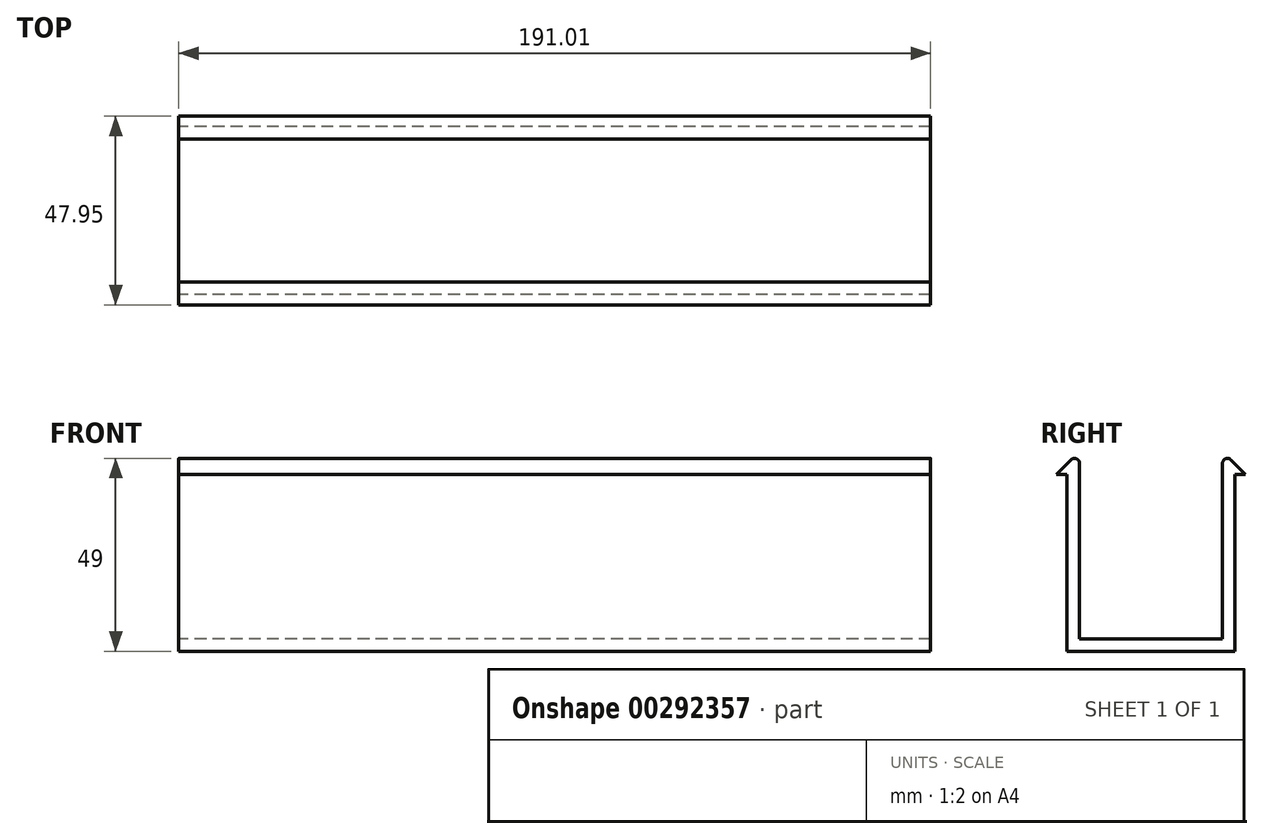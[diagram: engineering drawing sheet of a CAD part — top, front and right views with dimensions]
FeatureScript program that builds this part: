
annotation { "Feature Type Name" : "Feature", "Feature Type Description" : "" }
export const myFeature = defineFeature(function(context is Context, id is Id, definition is map)
    precondition{}
    {
        {
            var Q0;
            Q0=qCreatedBy(makeId("Right.planeOp"),FACE);
            var sketch = newSketch(context, id + "F0", { "sketchPlane" : qUnion([Q0])});
            skLineSegment(sketch, "E0", {"start": v(0, 0) * mm, "end": v(42.67, 0) * mm});
            skLineSegment(sketch, "E1", {"start": v(42.67, 0) * mm, "end": v(42.67, 44.98) * mm});
            skLineSegment(sketch, "E2", {"start": v(42.67, 44.98) * mm, "end": v(45.31, 44.98) * mm});
            skLineSegment(sketch, "E3", {"start": v(45.31, 44.98) * mm, "end": v(39.5, 50.8) * mm});
            skLineSegment(sketch, "E4", {"start": v(39.5, 50.8) * mm, "end": v(39.5, 3.18) * mm});
            skLineSegment(sketch, "E5", {"start": v(39.5, 3.18) * mm, "end": v(3.17, 3.17) * mm});
            skLineSegment(sketch, "E6", {"start": v(3.17, 3.17) * mm, "end": v(3.17, 50.8) * mm});
            skLineSegment(sketch, "E7", {"start": v(3.17, 50.8) * mm, "end": v(-2.64, 44.98) * mm});
            skLineSegment(sketch, "E8", {"start": v(-2.64, 44.98) * mm, "end": v(0, 44.98) * mm});
            skLineSegment(sketch, "E9", {"start": v(0, 44.98) * mm, "end": v(0, 0) * mm});
            skSolve(sketch);
        }
        {
            var Q0;
            Q0 = qSketchRegion(id + "F0", true);
            extrude(context, id + "F1", {"entities" : qUnion([Q0]), "depth" : 191 * mm});
        }
        {
            var Q0;
            Q0=makeQuery(id+"F1.opExtrude","SWEPT_EDGE",EDGE,{"disambiguationData":[OSD([sQuery(id+"F0.wireOp",EDGE,"E6"),sQuery(id+"F0.wireOp",EDGE,"E7")])]});
            var Q1;
            Q1=makeQuery(id+"F1.opExtrude","SWEPT_EDGE",EDGE,{"disambiguationData":[OSD([sQuery(id+"F0.wireOp",EDGE,"E3"),sQuery(id+"F0.wireOp",EDGE,"E4")])]});
            fillet(context, id + "F2", {"entities" : qUnion([Q0, Q1]), "radius" : 1.27 * mm, "tangentPropagation" : true, "allowEdgeOverflow" : false});
        }
    });
